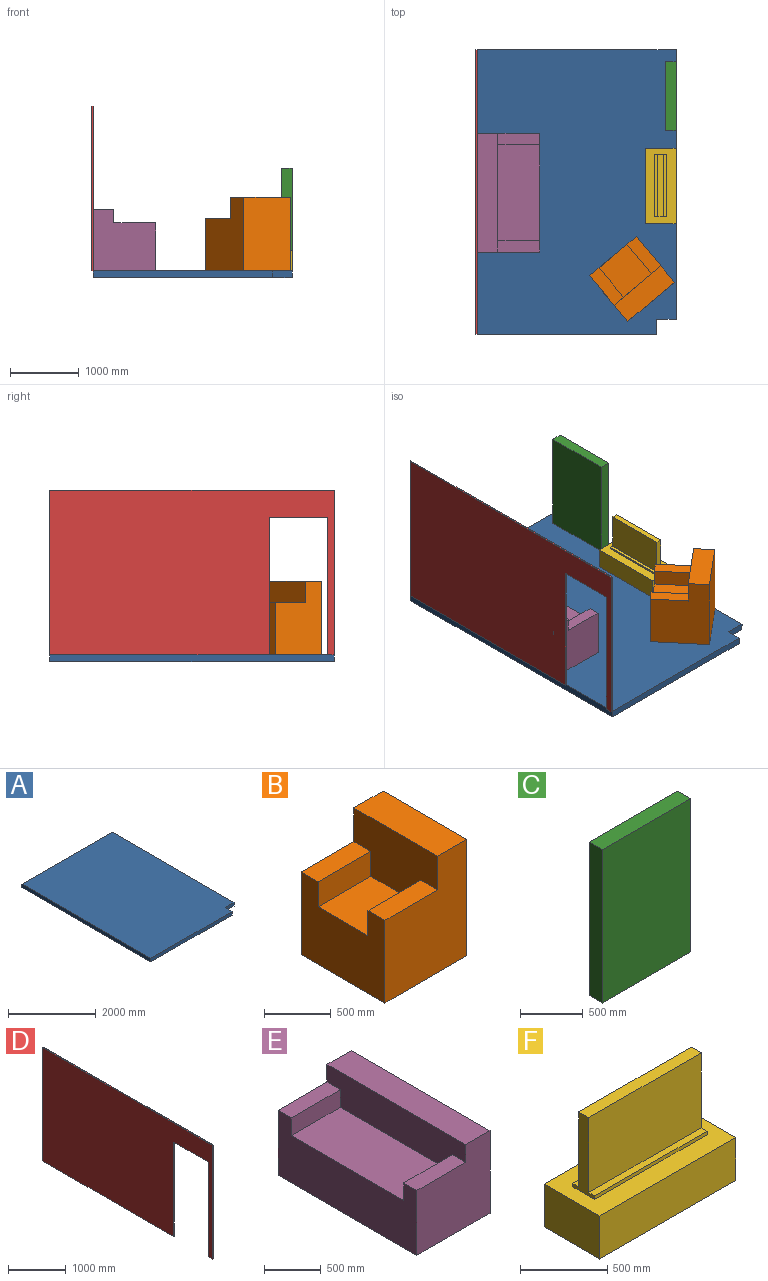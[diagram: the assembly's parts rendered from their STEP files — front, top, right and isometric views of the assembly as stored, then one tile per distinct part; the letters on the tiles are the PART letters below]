
ASSEMBLY  parts=6 mates=10
PART A: 8 faces, bbox 2900x4150x100 mm
  f0: plane 4150x100mm, normal (-1,0,0), area 415000mm2, adj f1,f5,f6,f7
  f1: plane 2620x100mm, normal (0,-1,0), area 262000mm2, adj f0,f2,f6,f7
  f2: plane 220x100mm, normal (1,0,0), area 22000mm2, adj f1,f3,f6,f7
  f3: plane 280x100mm, normal (0,-1,0), area 28000mm2, adj f2,f4,f6,f7
  f4: plane 3930x100mm, normal (1,0,0), area 393000mm2, adj f3,f5,f6,f7
  f5: plane 2900x100mm, normal (0,1,0), area 290000mm2, adj f0,f4,f6,f7
  f6: plane 4150x2900mm, normal (0,0,1), area 11973400mm2, adj f0,f1,f2,f3,f4,f5
  f7: plane 4150x2900mm, normal (0,0,-1), area 11973400mm2, adj f0,f1,f2,f3,f4,f5
PART B: 12 faces, bbox 870x890x1070 mm
  f0: plane 890x760mm, normal (-1,0,0), area 554500mm2, adj f1,f3,f5,f6,f7,f8,f10,f11
  f1: plane 1070x870mm, normal (0,1,0), area 757300mm2, adj f0,f2,f4,f5,f9,f11
  f2: plane 890x310mm, normal (0,0,1), area 275900mm2, adj f1,f3,f4,f9
  f3: plane 1070x870mm, normal (0,-1,0), area 757300mm2, adj f0,f2,f4,f5,f9,f10
  f4: plane 1070x890mm, normal (1,0,0), area 952300mm2, adj f1,f2,f3,f5
  f5: plane 890x870mm, normal (0,0,-1), area 774300mm2, adj f0,f1,f3,f4
  f6: plane 560x230mm, normal (0,-1,0), area 128800mm2, adj f0,f7,f9,f11
  f7: plane 560x530mm, normal (0,0,1), area 296800mm2, adj f0,f6,f8,f9
  f8: plane 560x230mm, normal (0,1,0), area 128800mm2, adj f0,f7,f9,f10
  f9: plane 890x540mm, normal (-1,0,0), area 397800mm2, adj f1,f2,f3,f6,f7,f8,f10,f11
  f10: plane 560x180mm, normal (0,0,1), area 100800mm2, adj f0,f3,f8,f9
  f11: plane 560x180mm, normal (0,0,1), area 100800mm2, adj f0,f1,f6,f9
PART C: 6 faces, bbox 1000x150x1500 mm
  f0: plane 1500x1000mm, normal (0,-1,0), area 1500000mm2, adj f1,f3,f4,f5
  f1: plane 1500x150mm, normal (1,0,0), area 225000mm2, adj f0,f2,f4,f5
  f2: plane 1500x1000mm, normal (0,1,0), area 1500000mm2, adj f1,f3,f4,f5
  f3: plane 1500x150mm, normal (-1,0,0), area 225000mm2, adj f0,f2,f4,f5
  f4: plane 1000x150mm, normal (0,0,1), area 150000mm2, adj f0,f1,f2,f3
  f5: plane 1000x150mm, normal (0,0,-1), area 150000mm2, adj f0,f1,f2,f3
PART D: 10 faces, bbox 20x4150x2400 mm
  f0: plane 3200x20mm, normal (0,0,-1), area 64000mm2, adj f1,f3,f4,f7
  f1: plane 4150x2400mm, normal (-1,0,0), area 8260000mm2, adj f0,f2,f4,f5,f6,f7,f8,f9
  f2: plane 2400x20mm, normal (0,-1,0), area 48000mm2, adj f1,f3,f5,f6
  f3: plane 4150x2400mm, normal (1,0,0), area 8260000mm2, adj f0,f2,f4,f5,f6,f7,f8,f9
  f4: plane 2400x20mm, normal (0,1,0), area 48000mm2, adj f0,f1,f3,f5
  f5: plane 4150x20mm, normal (0,0,1), area 83000mm2, adj f1,f2,f3,f4
  f6: plane 100x20mm, normal (0,0,-1), area 2000mm2, adj f1,f2,f3,f9
  f7: plane 2000x20mm, normal (0,-1,0), area 40000mm2, adj f0,f1,f3,f8
  f8: plane 850x20mm, normal (0,0,-1), area 17000mm2, adj f1,f3,f7,f9
  f9: plane 2000x20mm, normal (0,1,0), area 40000mm2, adj f1,f3,f6,f8
PART E: 12 faces, bbox 910x1730x890 mm
  f0: plane 910x890mm, normal (0,-1,0), area 694000mm2, adj f1,f2,f3,f5,f9,f11
  f1: plane 1730x700mm, normal (-1,0,0), area 945000mm2, adj f0,f4,f5,f6,f7,f8,f10,f11
  f2: plane 1730x300mm, normal (0,0,1), area 519000mm2, adj f0,f3,f4,f9
  f3: plane 1730x890mm, normal (1,0,0), area 1539700mm2, adj f0,f2,f4,f5
  f4: plane 910x890mm, normal (0,1,0), area 694000mm2, adj f1,f2,f3,f5,f9,f10
  f5: plane 1730x910mm, normal (0,0,-1), area 1574300mm2, adj f0,f1,f3,f4
  f6: plane 610x190mm, normal (0,1,0), area 115900mm2, adj f1,f8,f9,f11
  f7: plane 610x190mm, normal (0,-1,0), area 115900mm2, adj f1,f8,f9,f10
  f8: plane 1400x610mm, normal (0,0,1), area 854000mm2, adj f1,f6,f7,f9
  f9: plane 1730x380mm, normal (-1,0,0), area 594700mm2, adj f0,f2,f4,f6,f7,f8,f10,f11
  f10: plane 610x165mm, normal (0,0,1), area 100650mm2, adj f1,f4,f7,f9
  f11: plane 610x165mm, normal (0,0,1), area 100650mm2, adj f0,f1,f6,f9
PART F: 15 faces, bbox 1100x450x849 mm
  f0: plane 909x524mm, normal (0,-1,0), area 476316mm2, adj f2,f3,f4,f7
  f1: plane 909x524mm, normal (0,1,0), area 476316mm2, adj f2,f3,f4,f6
  f2: plane 549x176mm, normal (-1,0,0), area 46844mm2, adj f0,f1,f4,f5,f6,f7,f8,f14
  f3: plane 549x176mm, normal (1,0,0), area 46844mm2, adj f0,f1,f4,f5,f6,f7,f8,f14
  f4: plane 909x81mm, normal (0,0,1), area 73629mm2, adj f0,f1,f2,f3
  f5: plane 909x25mm, normal (0,1,0), area 22725mm2, adj f2,f3,f6,f14
  f6: plane 909x47.5mm, normal (0,0,1), area 43177.5mm2, adj f1,f2,f3,f5
  f7: plane 909x47.5mm, normal (0,0,1), area 43177.5mm2, adj f0,f2,f3,f8
  f8: plane 909x25mm, normal (0,-1,0), area 22725mm2, adj f2,f3,f7,f14
  f9: plane 450x300mm, normal (1,0,0), area 135000mm2, adj f10,f12,f13,f14
  f10: plane 1100x300mm, normal (0,-1,0), area 330000mm2, adj f9,f11,f13,f14
  f11: plane 450x300mm, normal (-1,0,0), area 135000mm2, adj f10,f12,f13,f14
  f12: plane 1100x300mm, normal (0,1,0), area 330000mm2, adj f9,f11,f13,f14
  f13: plane 1100x450mm, normal (0,0,-1), area 495000mm2, adj f9,f10,f11,f12
  f14: plane 1100x450mm, normal (0,0,1), area 335016mm2, adj f2,f3,f5,f8,f9,f10,f11,f12
PLACE A rot(axis=(-0.22,0.29,-0.93),0deg) t=(-1450,1855,0)mm
PLACE B rot(axis=(0,0,-1),50.1deg) t=(-642.01,586.82,100)mm
PLACE C rot(axis=(0.71,0.71,0),180deg) t=(0,3753.43,1600)mm
PLACE D rot(axis=(-0.13,0.1,-0.99),0deg) t=(-2910,1855,100)mm
PLACE E rot(axis=(0,0,1),180deg) t=(-2434.5,1844.85,100)mm
PLACE F rot(axis=(0,0,-1),90deg) t=(-225,1946.44,400)mm
MATE planar F.f12 <-> A.f4  axis (1,0,0) through (0,1946.44,250)mm
MATE planar A.f6 <-> B.f5  axis (0,0,1) through (-1450,3930,100)mm
MATE planar A.f6 <-> D.f0  axis (0,0,1) through (-1456.74,1865.11,100)mm
MATE planar A.f6 <-> E.f5  axis (0,0,1) through (-1456.74,1865.11,100)mm
MATE planar E.f3 <-> D.f3  axis (-1,0,0) through (-2900,1844.85,545)mm
MATE planar A.f6 <-> F.f13  axis (0,0,1) through (-1456.74,1865.11,100)mm
MATE planar A.f6 <-> C.f4  axis (0,0,1) through (-1456.74,1865.11,100)mm
MATE planar A.f1 <-> D.f2  axis (0,-1,0) through (-1590,-220,50)mm
MATE planar C.f2 <-> A.f4  axis (1,0,0) through (0,2753.43,850)mm
MATE planar D.f3 <-> A.f0  axis (1,0,0) through (-2900,2174.01,1341.16)mm
